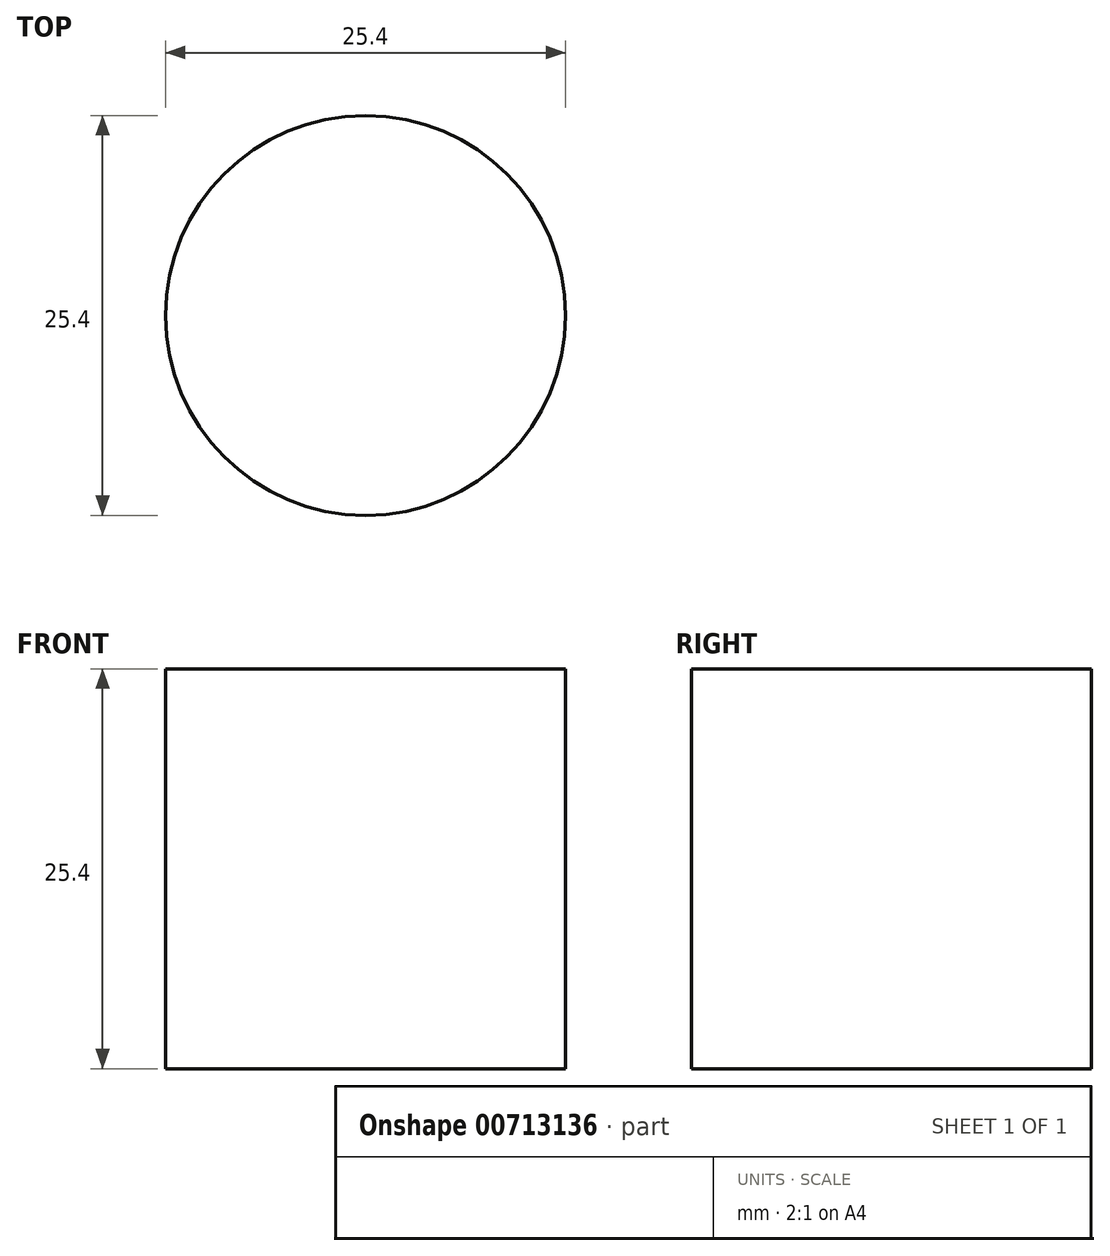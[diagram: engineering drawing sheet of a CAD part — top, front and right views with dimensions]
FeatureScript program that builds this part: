
annotation { "Feature Type Name" : "Feature", "Feature Type Description" : "" }
export const myFeature = defineFeature(function(context is Context, id is Id, definition is map)
    precondition{}
    {
        {
            var Q0;
            Q0=qCreatedBy(makeId("Top.planeOp"),FACE);
            var sketch = newSketch(context, id + "F0", { "sketchPlane" : qUnion([Q0])});
            skCircle(sketch, "E0", {"center": v(0, 1.57) * mm, "radius": 12.7 * mm});
            skSolve(sketch);
        }
        {
            var Q0;
            Q0 = qSketchRegion(id + "F0", true);
            extrude(context, id + "F1", {"entities" : qUnion([Q0]), "depth" : 25.4 * mm, "offsetDistance" : 25.4 * mm});
        }
    });
